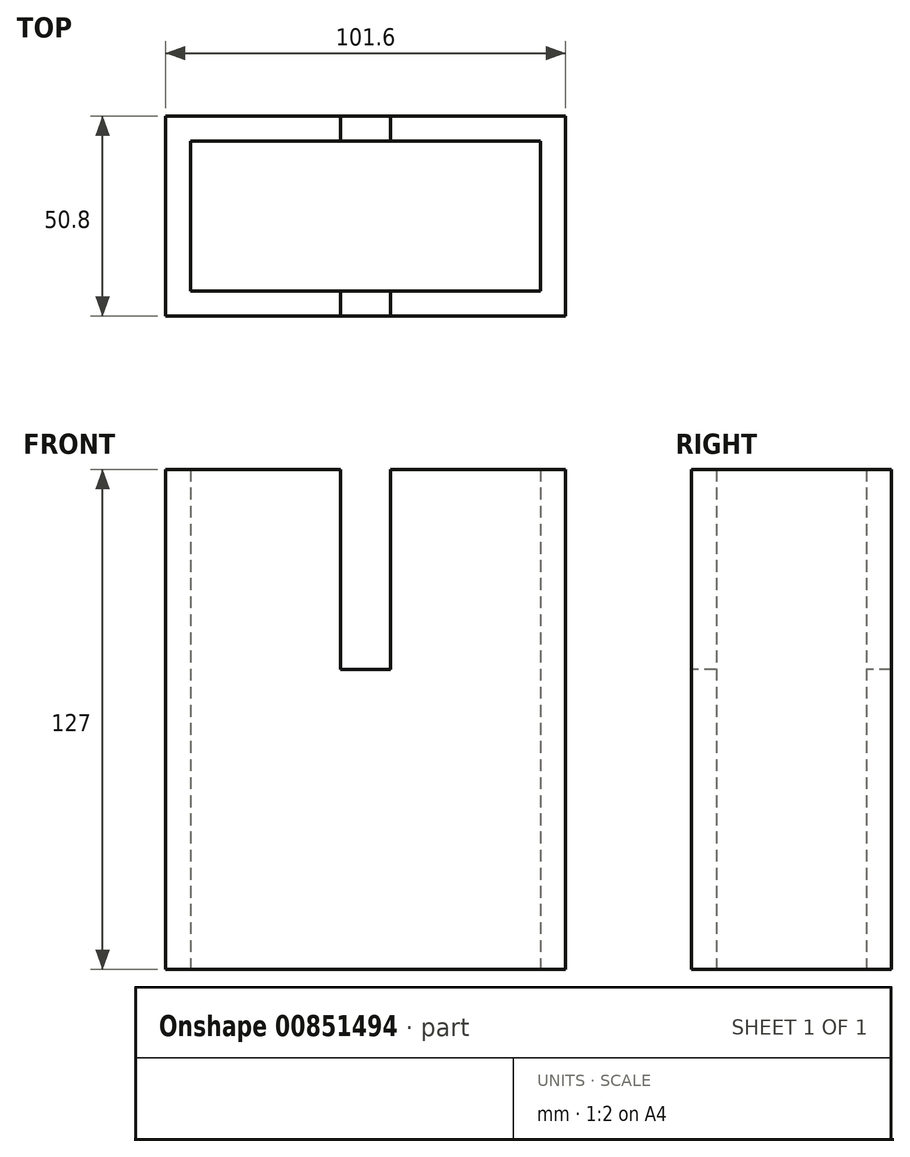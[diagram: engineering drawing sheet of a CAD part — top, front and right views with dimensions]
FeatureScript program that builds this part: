
annotation { "Feature Type Name" : "Feature", "Feature Type Description" : "" }
export const myFeature = defineFeature(function(context is Context, id is Id, definition is map)
    precondition{}
    {
        {
            var Q0;
            Q0=qCreatedBy(makeId("Top.planeOp"),FACE);
            var sketch = newSketch(context, id + "F0", { "sketchPlane" : qUnion([Q0])});
            skLineSegment(sketch, "E0.bottom", {"start": v(-50.8, 25.4) * mm, "end": v(50.8, 25.4) * mm});
            skLineSegment(sketch, "E0.top", {"start": v(-50.8, -25.4) * mm, "end": v(50.8, -25.4) * mm});
            skLineSegment(sketch, "E0.left", {"start": v(-50.8, 25.4) * mm, "end": v(-50.8, -25.4) * mm});
            skLineSegment(sketch, "E0.right", {"start": v(50.8, 25.4) * mm, "end": v(50.8, -25.4) * mm});
            skLineSegment(sketch, "E1.bottom", {"start": v(-44.45, 19.05) * mm, "end": v(44.45, 19.05) * mm});
            skLineSegment(sketch, "E1.top", {"start": v(-44.45, -19.05) * mm, "end": v(44.45, -19.05) * mm});
            skLineSegment(sketch, "E1.left", {"start": v(-44.45, 19.05) * mm, "end": v(-44.45, -19.05) * mm});
            skLineSegment(sketch, "E1.right", {"start": v(44.45, 19.05) * mm, "end": v(44.45, -19.05) * mm});
            skSolve(sketch);
        }
        {
            var Q0;
            Q0=makeQuery(id+"F0.imprint","IMPRINT",FACE,{"disambiguationData":[TD([[makeQuery(id+"F0.imprint","IMPRINT",EDGE,{"derivedFrom":sQuery(id+"F0.wireOp",EDGE,"E0.bottom")}),-1.0]])]});
            extrude(context, id + "F1", {"entities" : qUnion([Q0]), "depth" : 127 * mm, "offsetDistance" : 25.4 * mm});
        }
        {
            var Q0;
            Q0=qCreatedBy(makeId("Right.planeOp"),FACE);
            var sketch = newSketch(context, id + "F2", { "sketchPlane" : qUnion([Q0])});
            skLineSegment(sketch, "E2.bottom", {"start": v(31.75, 152.4) * mm, "end": v(-44.45, 152.4) * mm});
            skLineSegment(sketch, "E2.top", {"start": v(31.75, 76.2) * mm, "end": v(-44.45, 76.2) * mm});
            skLineSegment(sketch, "E2.left", {"start": v(31.75, 152.4) * mm, "end": v(31.75, 76.2) * mm});
            skLineSegment(sketch, "E2.right", {"start": v(-44.45, 152.4) * mm, "end": v(-44.45, 76.2) * mm});
            skSolve(sketch);
        }
        {
            var Q0;
            Q0=makeQuery(id+"F2.imprint","IMPRINT",FACE,{"disambiguationData":[TD([[makeQuery(id+"F2.imprint","IMPRINT",EDGE,{"derivedFrom":sQuery(id+"F2.wireOp",EDGE,"E2.bottom")}),1.0]])]});
            extrude(context, id + "F3", {"entities" : qUnion([Q0]), "operationType" : NewBodyOperationType.REMOVE, "oppositeDirection" : true, "depth" : 12.7 * mm, "offsetDistance" : 25.4 * mm, "symmetric" : true});
        }
    });
